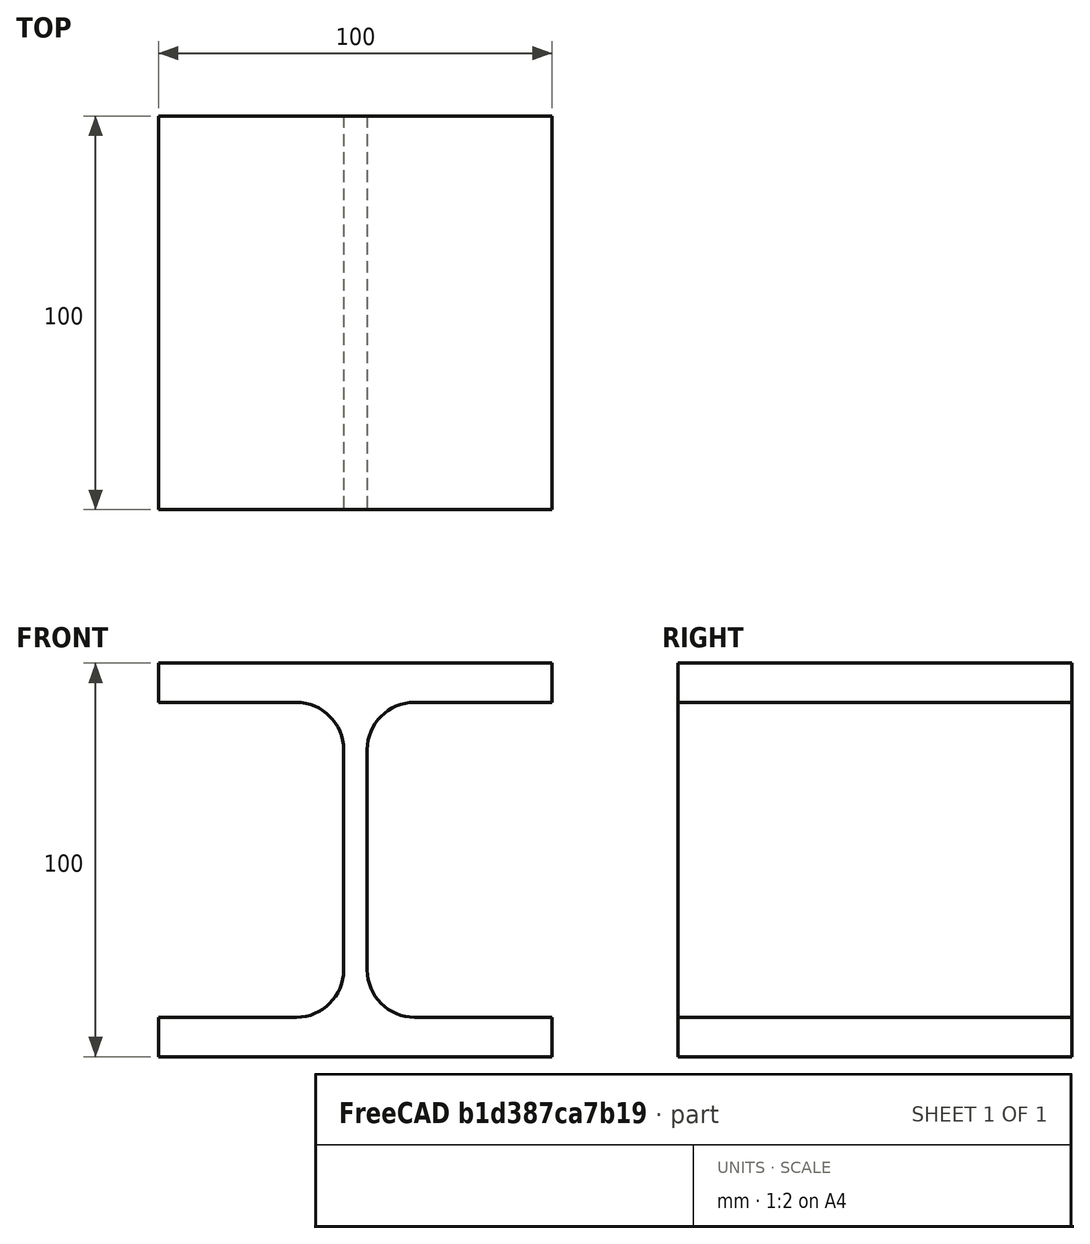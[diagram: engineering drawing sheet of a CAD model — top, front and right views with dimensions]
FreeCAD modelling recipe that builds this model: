
FCSTD DOCUMENT  (FreeCAD 0.21R33694 (Git))
Label: Profile HEB
License: All rights reserved
LicenseURL: http://en.wikipedia.org/wiki/All_rights_reserved
objects: Sketcher::SketchObject×1, Spreadsheet::Sheet×1, PartDesign::Pad×1, PartDesign::Body×1
note: 4 computed .brp shape members not serialized (recipe doc carries the construction recipe); baked Part::Feature solids carry a one-line shape summary decoded from their .brp

FEATURE [Sketcher::SketchObject] Sketch  label="Sk_HEB"
  AttacherType = A
  FullyConstrained = true
  Placement = pos=(0,0,0) rot=(1,0,0;1.5708rad)
  expr: .Constraints.bb = Spreadsheet.HEB_b
  expr: .Constraints.e1 = Spreadsheet.HEB_e1
  expr: .Constraints.ee = Spreadsheet.HEB_e
  expr: .Constraints.hh = Spreadsheet.HEB_h
  expr: .Constraints.rr = Spreadsheet.HEB_r
  sketch-geometry (16):
    g0: ArcOfCircle CenterX=-15 CenterY=-28 CenterZ=0 NormalX=0 NormalY=0 NormalZ=1 AngleXU=0 Radius=12 StartAngle=4.71239 EndAngle=6.28319
    g1: ArcOfCircle CenterX=15 CenterY=-28 CenterZ=0 NormalX=0 NormalY=0 NormalZ=1 AngleXU=0 Radius=12 StartAngle=3.14159 EndAngle=4.71239
    g2: ArcOfCircle CenterX=15 CenterY=28 CenterZ=0 NormalX=0 NormalY=0 NormalZ=1 AngleXU=0 Radius=12 StartAngle=1.5708 EndAngle=3.14159
    g3: ArcOfCircle CenterX=-15 CenterY=28 CenterZ=0 NormalX=0 NormalY=0 NormalZ=1 AngleXU=0 Radius=12 StartAngle=-9e-16 EndAngle=1.5708
    g4: LineSegment StartX=-50 StartY=-50 StartZ=0 EndX=50 EndY=-50 EndZ=0
    g5: LineSegment StartX=50 StartY=-50 StartZ=0 EndX=50 EndY=-40 EndZ=0
    g6: LineSegment StartX=-50 StartY=-50 StartZ=0 EndX=-50 EndY=-40 EndZ=0
    g7: LineSegment StartX=-50 StartY=-40 StartZ=0 EndX=-15 EndY=-40 EndZ=0
    g8: LineSegment StartX=50 StartY=-40 StartZ=0 EndX=15 EndY=-40 EndZ=0
    g9: LineSegment StartX=3 StartY=-28 StartZ=0 EndX=3 EndY=28 EndZ=0
    g10: LineSegment StartX=15 StartY=40 StartZ=0 EndX=50 EndY=40 EndZ=0
    g11: LineSegment StartX=50 StartY=40 StartZ=0 EndX=50 EndY=50 EndZ=0
    g12: LineSegment StartX=-50 StartY=40 StartZ=0 EndX=-15 EndY=40 EndZ=0
    g13: LineSegment StartX=-3 StartY=28 StartZ=0 EndX=-3 EndY=-28 EndZ=0
    g14: LineSegment StartX=-50 StartY=40 StartZ=0 EndX=-50 EndY=50 EndZ=0
    g15: LineSegment StartX=50 StartY=50 StartZ=0 EndX=-50 EndY=50 EndZ=0
  constraints (40):
    c: DistanceX(g4,g4) = 100  'bb'
    c: Radius(g0) = 12  'rr'
    c: DistanceX(g0,g1) = 6  'ee'
    c: DistanceY(g4,g11) = 100  'hh'
    c: DistanceY(g6,g6) = 10  'e1'
    c: Coincident(g10,g11)
    c: Coincident(g5,g8)
    c: Coincident(g4,g5)
    c: Coincident(g4,g6)
    c: Coincident(g6,g7)
    c: Symmetric(g6,g5,g-2)
    c: Symmetric(g12,g10,g-2)
    c: Horizontal(g4)
    c: Horizontal(g7)
    c: Equal(g7,g8)
    c: Equal(g8,g10)
    c: Equal(g10,g12)
    c: Tangent(g0,g7) = -1.5708
    c: Tangent(g0,g13) = 1.5708
    c: Tangent(g3,g13) = 1.5708
    c: Tangent(g3,g12) = 1.5708
    c: Tangent(g2,g10) = 1.5708
    c: Tangent(g2,g9) = 1.5708
    c: Tangent(g1,g9) = 1.5708
    c: Tangent(g1,g8) = 1.5708
    c: Equal(g6,g5)
    c: Equal(g5,g11)
    c: Vertical(g6)
    c: Vertical(g11)
    c: Horizontal(g12)
    c: Horizontal(g10)
    c: Horizontal(g8)
    c: Symmetric(g0,g1,g-2)
    c: Symmetric(g2,g1,g-1)
    c: Equal(g1,g2)
    c: Coincident(g14,g12)
    c: Vertical(g14)
    c: Coincident(g15,g11)
    c: Coincident(g15,g14)
    c: Horizontal(g15)
FEATURE [Spreadsheet::Sheet] Spreadsheet  label="Sp_HEB"
  cells = A1='HEB 100; B1(HEB_h)==.B2; C1(HEB_b)==.C2; D1(HEB_e)==.D2; E1(HEB_e1)==.E2; F1(HEB_r)==.F2; G1(HEB_Label)==.G2; A2(HEA_100)='HEB 100; B2=100; C2=100; D2=6; E2=10; F2=12; G2='HEB 100; A3(HEA_120)='HEB 120; B3=120; C3=120; D3=6.5; E3=11; F3=12; G3='HEB 120; A4(HEA_140)='HEB 140; B4=140; C4=140; D4=7; E4=12; F4=12; G4='HEB 140; A5(HEA_160)='HEB 160; B5=160; C5=160; D5=8; E5=13; F5=15; G5='HEB 160; A6(HEA_180)='HEB 180; B6=180; C6=180; D6=8.5; E6=14; F6=15; G6='HEB 180; A7(HEA_200)='HEB 200; B7=200; C7=200; D7=9; E7=15; F7=18; G7='HEB 200; A8(HEA_220)='HEB 220; B8=220; C8=220; D8=9.5; E8=16; F8=18; G8='HEB 220; A9(HEA_240)='HEB 240; B9=240; C9=240; D9=10; E9=17; F9=21; G9='HEB 240; A10(HEA_260)='HEB 260; B10=260; C10=260; D10=10; E10=17.5; F10=24; G10='HEB 260; A11(HEA_280)='HEB 280; B11=280; C11=280; D11=10.5; E11=18; F11=24; G11='HEB 280; A12(HEA_300)='HEB 300; B12=300; C12=300; D12=11; E12=19; F12=27; G12='HEB 300; A13='HEB 320; B13=320; C13=300; D13=11.5; E13=20.5; F13=27; G13='HEB 320; A14='HEB 340; B14=340; C14=300; D14=12; E14=21.5; F14=27; G14='HEB 340; A15='HEB 360; B15=360; C15=300; D15=12.5; E15=22.5; F15=27; G15='HEB 360; A16='HEB 400; B16=400; C16=300; D16=13.5; E16=24; F16=27; G16='HEB 400; A17='HEB 450; B17=450; C17=300; D17=14; E17=26; F17=27; G17='HEB 450; A18='HEB 500; B18=500; C18=300; D18=14.5; E18=28; F18=27; G18='HEB 500; A19='HEB 550; B19=550; C19=300; D19=15; E19=29; F19=27; G19='HEB 550; A20='HEB 600; B20=600; C20=300; D20=15.5; E20=30; F20=27; G20='HEB 600; A21='HEB 650; B21=650; C21=300; D21=16; E21=31; F21=27; G21='HEB 650; A22='HEB 700; B22=700; C22=300; D22=17; E22=32; F22=27; G22='HEB 700; A23='HEB 800; B23=800; C23=300; D23=17.5; E23=33; F23=30; G23='HEB 800; A24='HEB 900; B24=900; C24=300; D24=18.5; E24=35; F24=30; G24='HEB 900; A25='HEB 1000; B25=1000; C25=300; D25=19; E25=36; F25=30; G25='HEB 1000
  expr: .cells.Bind.B1.ZZ1 = tuple(.cells; <<B>> + str(hiddenref(Body.Configuration) + 2); <<ZZ>> + str(hiddenref(Body.Configuration) + 2))
FEATURE [PartDesign::Pad] Pad
  Direction = (0,-1,2e-16)
  Length = 100
  Length2 = 10
  Placement = pos=(0,0,0) rot=(1,0,0;1.5708rad)
  Profile = -> Sketch
  ReferenceAxis = -> Sketch [N_Axis]
  Type = 0
FEATURE [PartDesign::Body] Body  label="HEB 100"
  Configuration = 0
  Group = -> [Sketch,Pad]
  Origin = -> Origin
  Tip = -> Pad
  expr: .Configuration.Enum = Spreadsheet.cells[<<A2:|>>]
  expr: Label = Spreadsheet.HEB_Label
